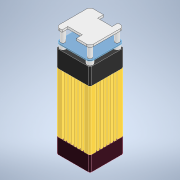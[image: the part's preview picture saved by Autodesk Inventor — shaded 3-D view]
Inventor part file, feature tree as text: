
AUTODESK INVENTOR PART (.ipt)
format: ipt  version: 2022.2 (Build 262287010, 287A)  size: 456,192 bytes
history: native  units: mm
features: sketch x17, extrude x14, fillet x4, hole x3, plane x2, pattern_linear x2, mirror x1
ambient origin geometry x8: Origin, YZ Plane, XZ Plane, XY Plane, X Axis, Y Axis, Z Axis, Center Point
bodies: Volumenkörper1 (feature_tree), Volumenkörper2 (feature_tree), Volumenkörper3 (feature_tree), Volumenkörper4 (feature_tree), Volumenkörper5 (feature_tree), Volumenkörper6 (feature_tree), Volumenkörper7 (feature_tree)
feature tree (43):
  extrude  "Extrusion1"  Depth=40.0mm
  extrude  "Extrusion2"  Depth=70.0mm TaperAngle=0.0deg
  extrude  "Extrusion3"  Depth=2.0mm
  fillet  "Rundung1"  Radius=32.0mm
  extrude  "Extrusion4"  Depth=7.0mm
  plane  "Arbeitsebene1"
  extrude  "Extrusion5"  Depth=5.0mm
  extrude  "Extrusion6"  Depth=5.0mm
  plane  "Arbeitsebene2"
  extrude  "Extrusion7"  Depth=12.7mm
  extrude  "Extrusion8"  Depth=40.0mm
  extrude  "Extrusion9"  Depth=36.0mm
  extrude  "Extrusion10"  Depth=16.0mm TaperAngle=0.0deg
  extrude  "Extrusion11"  Depth=16.0mm TaperAngle=0.0deg
  pattern_linear  "Rechteckige Anordnung1"  Spacing1=2.0mm  [1 undecoded]
  extrude  "Extrusion12"  Depth=70.0mm TaperAngle=0.0deg
  pattern_linear  "Rechteckige Anordnung2"  Count1=4 Spacing1=4.0mm
  mirror  "Spiegeln1"
  fillet  "Rundung2"  Radius=40.0mm
  fillet  "Rundung3"  Radius=2.0mm
  fillet  "Rundung4"  Radius=4.0mm
  extrude  "Extrusion13"  Depth=70.0mm TaperAngle=0.0deg
  hole  "Bohrung1"  [1 undecoded]
  hole  "Bohrung2"  [1 undecoded]
  hole  "Bohrung3"  [1 undecoded]
  extrude  "Extrusion14"  Depth=2.0mm
  sketch  "Skizze1"  dims[d0=40.0mm d1=40.0mm]
  sketch  "Skizze2"  dims[d2=18.0mm d3=0.0mm d4=70.0mm d5=0.0mm]
  sketch  "Skizze3"  dims[d6=20.0mm d7=0.0mm d8=2.0mm d9=32.0mm]
  sketch  "Skizze4"  dims[d10=32.0mm d11=7.0mm]
  sketch  "Skizze5"  dims[d12=5.0mm d13=0.0mm d14=5.0mm]
  sketch  "Skizze6"  dims[d15=1.5mm d16=0.0mm d17=5.0mm]
  sketch  "Skizze7"  dims[d18=12.7mm d19=0.0mm d20=12.7mm]
  sketch  "Skizze8"  dims[d21=40.0mm d22=40.0mm]
  sketch  "Skizze9"  dims[d23=2.5mm d24=0.0mm d25=36.0mm]
  sketch  "Skizze10"  dims[d26=36.0mm d27=16.0mm d28=0.0mm]
  sketch  "Skizze11"  dims[d29=12.0mm d30=16.0mm d31=0.0mm]
  sketch  "Skizze12"  dims[d32=4.0mm]
  sketch  "Skizze13"  dims[d34=8.0mm]
  sketch  "Skizze14"  dims[d36=8.0mm]
  sketch  "Skizze15"  dims[d37=4.0mm]
  sketch  "Skizze16"  dims[d38=2.0mm d39=0.0mm]
  sketch  "Skizze17"  dims[d40=4.0mm d41=2.0mm d42=70.0mm d43=0.0mm d44=40.0mm d46=4.0mm d47=40.0mm d49=4.0mm d50=2.0mm d51=4.0mm d52=70.0mm d53=0.0mm d54=40.0mm d56=4.0mm d57=40.0mm d59=4.0mm d60=4.0mm d61=2.0mm d62=1.0mm d63=7.0mm d64=17.0mm d65=7.0mm d66=17.0mm d67=7.0mm d68=7.0mm d69=70.0mm d70=0.0mm d71=10.0mm d72=20.0mm d73=13.0mm d74=2.459mm d75=6.0mm d76=6.0mm d77=4.9mm d78=14.3117mm d79=8.8mm d80=20.594885mm d81=5.0mm d82=10.0mm d83=8.0mm d84=2.459mm d85=6.0mm d86=4.0mm d87=2.0mm d88=90.0deg d89=8.8mm d90=20.594885mm d91=40.0mm d92=10.0mm d93=8.0mm d94=5.0mm d95=2.459mm d96=6.0mm d97=4.0mm d98=2.0mm d99=90.0deg d100=8.8mm d101=20.594885mm d102=8.0mm d103=1.0mm d104=0.0mm]
note: 4 required parameter values undecoded (feature->parameter linkage not recoverable at this tier; creation-order binding heuristic only, values carry confidence <= 0.55)
